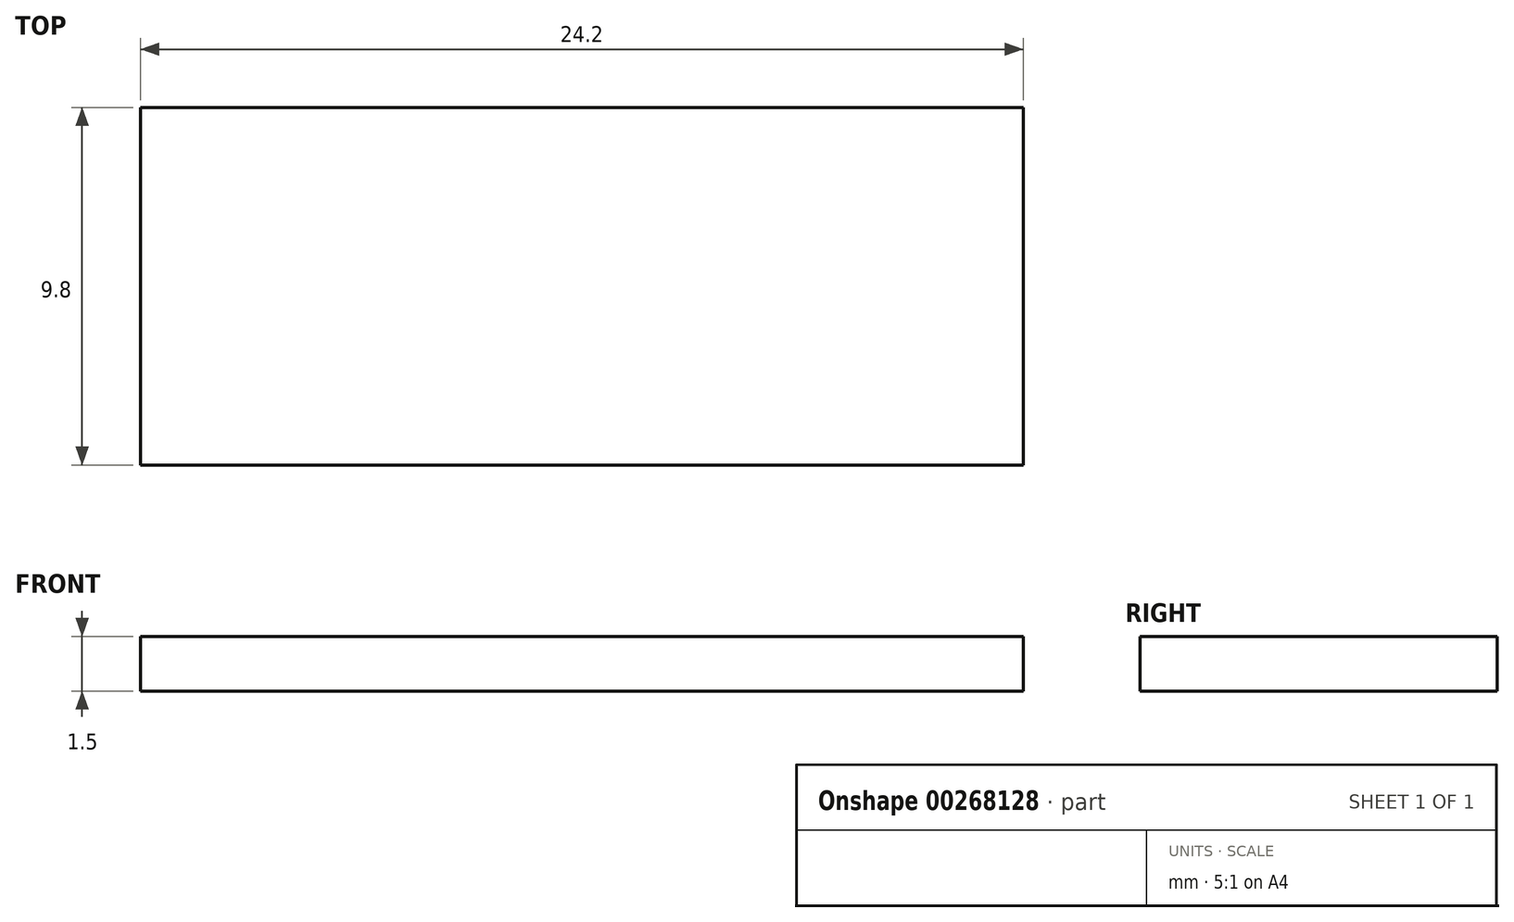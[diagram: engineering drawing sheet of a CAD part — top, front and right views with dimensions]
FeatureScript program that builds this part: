
annotation { "Feature Type Name" : "Feature", "Feature Type Description" : "" }
export const myFeature = defineFeature(function(context is Context, id is Id, definition is map)
    precondition{}
    {
        {
            var Q0;
            Q0=qCreatedBy(makeId("Top.planeOp"),FACE);
            var sketch = newSketch(context, id + "F0", { "sketchPlane" : qUnion([Q0])});
            skLineSegment(sketch, "E0.bottom", {"start": v(-12.1, 4.9) * mm, "end": v(12.1, 4.9) * mm});
            skLineSegment(sketch, "E0.top", {"start": v(-12.1, -4.9) * mm, "end": v(12.1, -4.9) * mm});
            skLineSegment(sketch, "E0.left", {"start": v(-12.1, 4.9) * mm, "end": v(-12.1, -4.9) * mm});
            skLineSegment(sketch, "E0.right", {"start": v(12.1, 4.9) * mm, "end": v(12.1, -4.9) * mm});
            skPoint(sketch, "E0.middle", {"position": v(0, 0) * mm});
            skSolve(sketch);
        }
        {
            var Q0;
            Q0=makeQuery(id+"F0.imprint","IMPRINT",FACE,{"disambiguationData":[TD([[makeQuery(id+"F0.imprint","IMPRINT",EDGE,{"derivedFrom":sQuery(id+"F0.wireOp",EDGE,"E0.bottom")}),-1.0]])]});
            extrude(context, id + "F1", {"entities" : qUnion([Q0]), "depth" : 1.5 * mm, "offsetDistance" : 25 * mm});
        }
    });
